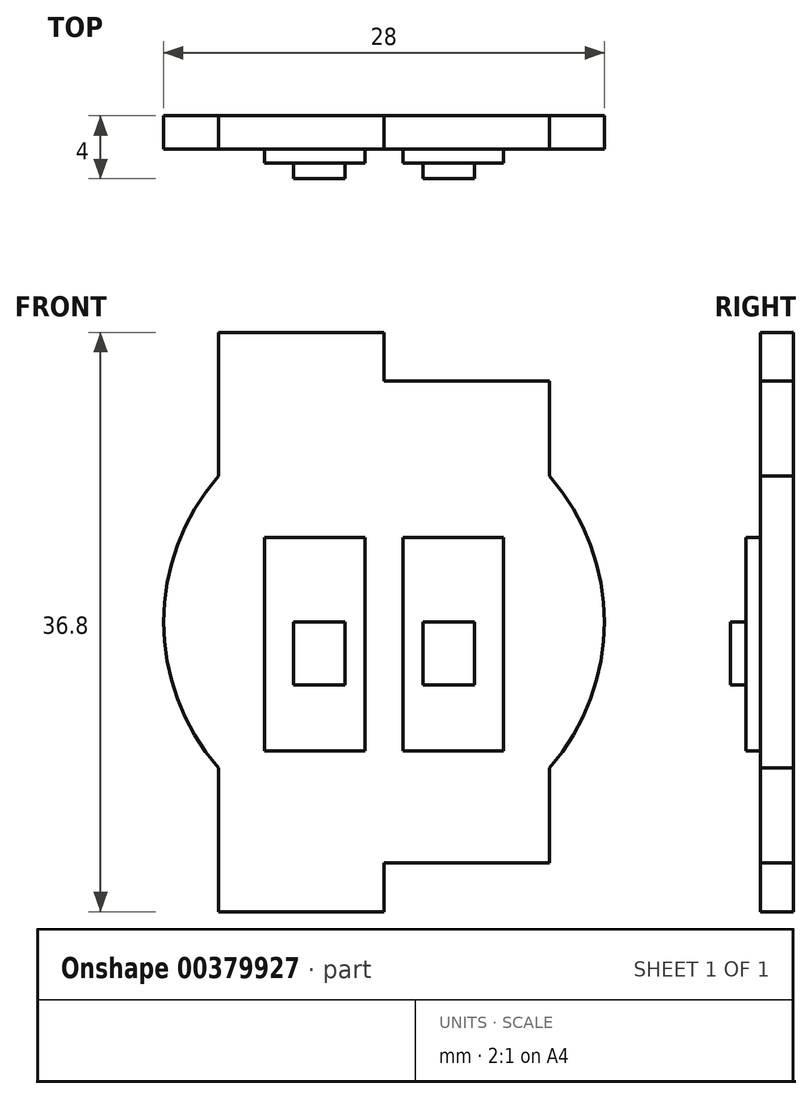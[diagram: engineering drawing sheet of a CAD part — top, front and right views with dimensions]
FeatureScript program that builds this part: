
annotation { "Feature Type Name" : "Feature", "Feature Type Description" : "" }
export const myFeature = defineFeature(function(context is Context, id is Id, definition is map)
    precondition{}
    {
        {
            var Q0;
            Q0=qCreatedBy(makeId("Front.planeOp"),FACE);
            var sketch = newSketch(context, id + "F0", { "sketchPlane" : qUnion([Q0])});
            skArc(sketch, "E0", {"start": v(-10.5, 9.26) * mm, "mid": v(-14, 0) * mm, "end": v(-10.5, -9.26) * mm});
            skLineSegment(sketch, "E1", {"start": v(0, 18.4) * mm, "end": v(-10.5, 18.4) * mm});
            skLineSegment(sketch, "E2", {"start": v(-10.5, 18.4) * mm, "end": v(-10.5, 9.26) * mm});
            skLineSegment(sketch, "E3", {"start": v(0, 18.4) * mm, "end": v(0, 15.3) * mm});
            skLineSegment(sketch, "E4", {"start": v(0, 15.3) * mm, "end": v(10.5, 15.3) * mm});
            skLineSegment(sketch, "E5", {"start": v(10.5, 15.3) * mm, "end": v(10.5, 9.26) * mm});
            skArc(sketch, "E6.trimOffspring", {"start": v(10.5, -9.26) * mm, "mid": v(14, 0) * mm, "end": v(10.5, 9.26) * mm});
            skPoint(sketch, "E7.orphan", {"position": v(-10.5, -16.8) * mm});
            skPoint(sketch, "E8.trimOffspring.end.orphan", {"position": v(10.5, -16.8) * mm});
            skLineSegment(sketch, "E9.MirrorCS", {"start": v(-10.5, -18.4) * mm, "end": v(-10.5, -9.26) * mm});
            skLineSegment(sketch, "E10.MirrorCS", {"start": v(10.5, -15.3) * mm, "end": v(10.5, -9.26) * mm});
            skLineSegment(sketch, "E11.MirrorCS", {"start": v(0, -15.3) * mm, "end": v(10.5, -15.3) * mm});
            skLineSegment(sketch, "E12.MirrorCS", {"start": v(0, -18.4) * mm, "end": v(-10.5, -18.4) * mm});
            skPoint(sketch, "E13.orphan", {"position": v(-10.5, 9.26) * mm});
            skLineSegment(sketch, "E14", {"start": v(0, -15.3) * mm, "end": v(0, -18.4) * mm});
            skSolve(sketch);
        }
        {
            var Q0;
            Q0=makeQuery(id+"F0.imprint","IMPRINT",FACE,{"disambiguationData":[TD([[makeQuery(id+"F0.imprint","IMPRINT",EDGE,{"derivedFrom":sQuery(id+"F0.wireOp",EDGE,"E0")}),1.0]])]});
            var sketch = newSketch(context, id + "F1", { "sketchPlane" : qUnion([Q0])});
            skLineSegment(sketch, "E15", {"start": v(-7.58, 5.38) * mm, "end": v(-1.22, 5.38) * mm});
            skLineSegment(sketch, "E16", {"start": v(-1.22, 5.38) * mm, "end": v(-1.22, -8.18) * mm});
            skLineSegment(sketch, "E17", {"start": v(-1.22, -8.18) * mm, "end": v(-7.58, -8.18) * mm});
            skLineSegment(sketch, "E18", {"start": v(-7.58, -8.18) * mm, "end": v(-7.58, 5.38) * mm});
            skLineSegment(sketch, "E19.MirrorCS", {"start": v(7.58, 5.38) * mm, "end": v(1.22, 5.38) * mm});
            skLineSegment(sketch, "E20.MirrorCS", {"start": v(7.58, -8.18) * mm, "end": v(7.58, 5.38) * mm});
            skLineSegment(sketch, "E21.MirrorCS", {"start": v(1.22, 5.38) * mm, "end": v(1.22, -8.18) * mm});
            skLineSegment(sketch, "E22.MirrorCS", {"start": v(1.22, -8.18) * mm, "end": v(7.58, -8.18) * mm});
            skLineSegment(sketch, "E23", {"start": v(-5.74, 0) * mm, "end": v(-5.74, -4) * mm});
            skLineSegment(sketch, "E24", {"start": v(-5.74, -4) * mm, "end": v(-2.47, -4) * mm});
            skLineSegment(sketch, "E25", {"start": v(-2.47, -4) * mm, "end": v(-2.47, 0) * mm});
            skLineSegment(sketch, "E26", {"start": v(-2.47, 0) * mm, "end": v(-5.74, 0) * mm});
            skLineSegment(sketch, "E27.MirrorCS", {"start": v(2.47, 0) * mm, "end": v(5.74, 0) * mm});
            skLineSegment(sketch, "E28.MirrorCS", {"start": v(5.74, 0) * mm, "end": v(5.74, -4) * mm});
            skLineSegment(sketch, "E29.MirrorCS", {"start": v(2.47, -4) * mm, "end": v(2.47, 0) * mm});
            skLineSegment(sketch, "E30.MirrorCS", {"start": v(5.74, -4) * mm, "end": v(2.47, -4) * mm});
            skSolve(sketch);
        }
        {
            var Q0;
            Q0 = qSketchRegion(id + "F0", true);
            extrude(context, id + "F2", {"entities" : qUnion([Q0]), "depth" : 2.1 * mm});
        }
        {
            var Q0;
            Q0=makeQuery(id+"F1.imprint","IMPRINT",FACE,{"disambiguationData":[TD([[makeQuery(id+"F1.imprint","IMPRINT",EDGE,{"derivedFrom":sQuery(id+"F1.wireOp",EDGE,"E15")}),-1.0]])]});
            var Q1;
            Q1=makeQuery(id+"F1.imprint","IMPRINT",FACE,{"disambiguationData":[TD([[makeQuery(id+"F1.imprint","IMPRINT",EDGE,{"derivedFrom":sQuery(id+"F1.wireOp",EDGE,"E19.MirrorCS")}),1.0]])]});
            extrude(context, id + "F3", {"entities" : qUnion([Q0, Q1]), "operationType" : NewBodyOperationType.ADD, "depth" : 3 * mm});
        }
        {
            var Q0;
            Q0=makeQuery(id+"F1.imprint","IMPRINT",FACE,{"disambiguationData":[TD([[makeQuery(id+"F1.imprint","IMPRINT",EDGE,{"derivedFrom":sQuery(id+"F1.wireOp",EDGE,"E23")}),1.0]])]});
            var Q1;
            Q1=makeQuery(id+"F1.imprint","IMPRINT",FACE,{"disambiguationData":[TD([[makeQuery(id+"F1.imprint","IMPRINT",EDGE,{"derivedFrom":sQuery(id+"F1.wireOp",EDGE,"E27.MirrorCS")}),-1.0]])]});
            extrude(context, id + "F4", {"entities" : qUnion([Q0, Q1]), "operationType" : NewBodyOperationType.ADD, "depth" : 4 * mm});
        }
    });
